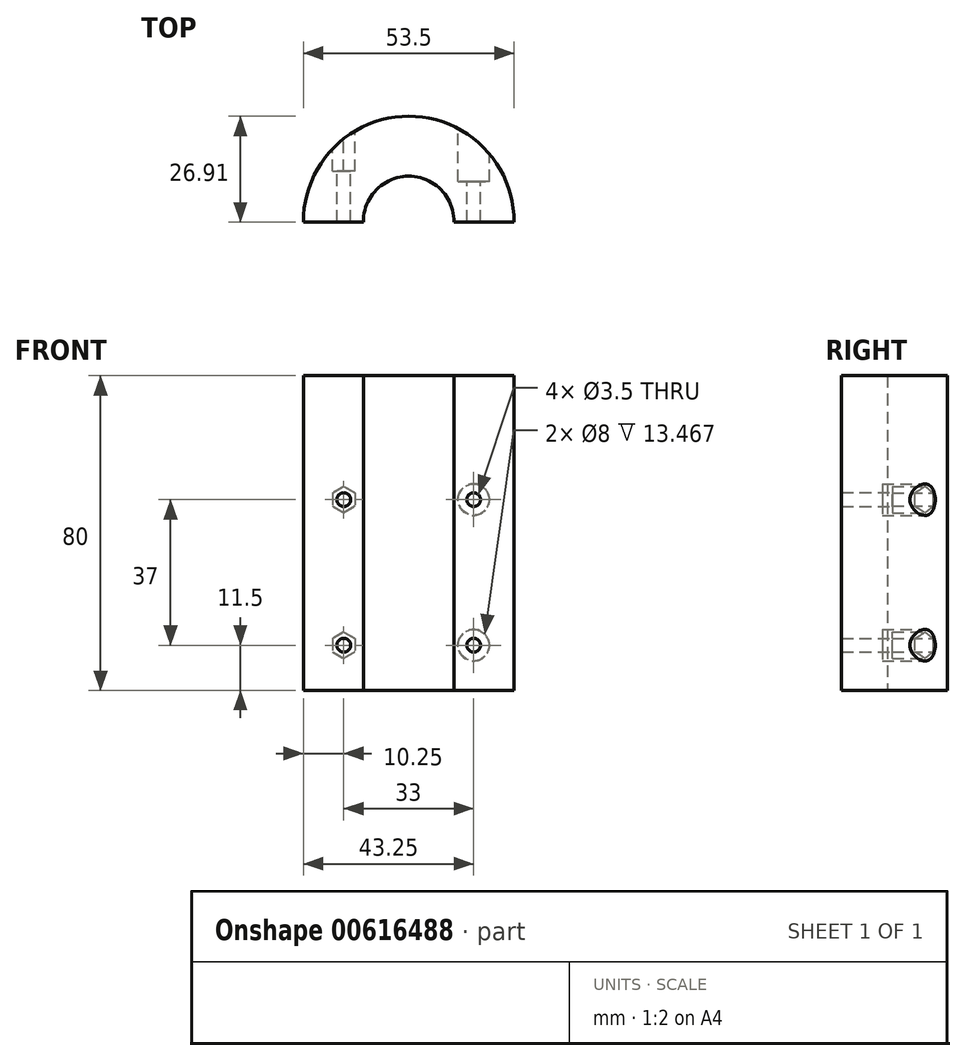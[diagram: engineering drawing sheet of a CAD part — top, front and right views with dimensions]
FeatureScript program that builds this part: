
annotation { "Feature Type Name" : "Feature", "Feature Type Description" : "" }
export const myFeature = defineFeature(function(context is Context, id is Id, definition is map)
    precondition{}
    {
        {
            var Q0;
            Q0=qCreatedBy(makeId("Top.planeOp"),FACE);
            var sketch = newSketch(context, id + "F0", { "sketchPlane" : qUnion([Q0])});
            skArc(sketch, "E0", {"start": v(26.75, -0.16) * mm, "mid": v(0, 26.75) * mm, "end": v(-26.75, -0.16) * mm});
            skArc(sketch, "E1", {"start": v(11.5, -0.16) * mm, "mid": v(0, 11.5) * mm, "end": v(-11.5, -0.16) * mm});
            skLineSegment(sketch, "E2", {"start": v(-26.75, -0.16) * mm, "end": v(-11.5, -0.16) * mm});
            skLineSegment(sketch, "E3.trimOffspring", {"start": v(11.5, -0.16) * mm, "end": v(26.75, -0.16) * mm});
            skSolve(sketch);
        }
        {
            var Q0;
            Q0 = qSketchRegion(id + "F0", true);
            extrude(context, id + "F1", {"entities" : qUnion([Q0]), "depth" : 80 * mm, "offsetDistance" : 25 * mm});
        }
        {
            var Q0;
            Q0=qCreatedBy(makeId("Front.planeOp"),FACE);
            cPlane(context, id + "F2", {"entities" : qUnion([Q0]), "cplaneType" : CPlaneType.OFFSET, "offset" : 26.75 * mm, "oppositeDirection" : true, "width" : 150 * mm, "height" : 150 * mm});
        }
        {
            var Q0;
            Q0=qCreatedBy(id+"F2.planeOp",FACE);
            var sketch = newSketch(context, id + "F3", { "sketchPlane" : qUnion([Q0])});
            skLineSegment(sketch, "E4", {"start": v(0, 0) * mm, "end": v(0, 61.14) * mm, "construction": true});
            skLineSegment(sketch, "E5", {"start": v(19.91, 11.5) * mm, "end": v(-21.03, 11.5) * mm, "construction": true});
            skPoint(sketch, "E6", {"position": v(16.5, 11.5) * mm});
            skLineSegment(sketch, "E7", {"start": v(19.02, 30) * mm, "end": v(-19.41, 30) * mm, "construction": true});
            skPoint(sketch, "E8.MirrorP", {"position": v(16.5, 48.5) * mm});
            skPoint(sketch, "E9.MirrorP", {"position": v(-16.5, 48.5) * mm});
            skPoint(sketch, "E10.MirrorP", {"position": v(-16.5, 11.5) * mm});
            skCircle(sketch, "E11.cCircle", {"center": v(-16.5, 48.5) * mm, "radius": 2.9 * mm, "construction": true});
            skLineSegment(sketch, "E11.0", {"start": v(-13.6, 46.83) * mm, "end": v(-16.5, 45.15) * mm});
            skLineSegment(sketch, "E11.1", {"start": v(-16.5, 45.15) * mm, "end": v(-19.4, 46.83) * mm});
            skLineSegment(sketch, "E11.2", {"start": v(-19.4, 46.83) * mm, "end": v(-19.4, 50.17) * mm});
            skLineSegment(sketch, "E11.3", {"start": v(-19.4, 50.17) * mm, "end": v(-16.5, 51.85) * mm});
            skLineSegment(sketch, "E11.4", {"start": v(-16.5, 51.85) * mm, "end": v(-13.6, 50.17) * mm});
            skLineSegment(sketch, "E11.5", {"start": v(-13.6, 50.17) * mm, "end": v(-13.6, 46.83) * mm});
            skPoint(sketch, "E11.0.midPoint", {"position": v(-15.05, 45.99) * mm});
            skLineSegment(sketch, "E12.MirrorCS", {"start": v(-13.6, 9.83) * mm, "end": v(-13.6, 13.17) * mm});
            skLineSegment(sketch, "E13.MirrorCS", {"start": v(-13.6, 13.17) * mm, "end": v(-16.5, 14.85) * mm});
            skLineSegment(sketch, "E14.MirrorCS", {"start": v(-16.5, 8.15) * mm, "end": v(-13.6, 9.83) * mm});
            skLineSegment(sketch, "E15.MirrorCS", {"start": v(-19.4, 9.83) * mm, "end": v(-16.5, 8.15) * mm});
            skLineSegment(sketch, "E16.MirrorCS", {"start": v(-19.4, 13.17) * mm, "end": v(-19.4, 9.83) * mm});
            skLineSegment(sketch, "E17.MirrorCS", {"start": v(-16.5, 14.85) * mm, "end": v(-19.4, 13.17) * mm});
            skSolve(sketch);
        }
        {
            var Q0;
            Q0=sQuery(id+"F3.wireOp",VERTEX,"E8.MirrorP");
            var Q1;
            Q1=sQuery(id+"F3.wireOp",VERTEX,"E6");
            var Q2;
            Q2=makeQuery(id+"F1.opExtrude","SWEPT_BODY",BODY,{"disambiguationData":[OSD([sQuery(id+"F0.wireOp",EDGE,"E0"),sQuery(id+"F0.wireOp",EDGE,"E1"),sQuery(id+"F0.wireOp",EDGE,"E2"),sQuery(id+"F0.wireOp",EDGE,"E3.trimOffspring")])]});
            hole(context, id + "F4", {"style" : HoleStyle.C_BORE, "endStyle" : HoleEndStyle.THROUGH, "oppositeDirection" : true, "holeDiameter" : 3.5 * mm, "cBoreDiameter" : 8 * mm, "cBoreDepth" : 7 * mm, "majorDiameter" : 5 * mm, "isTappedThrough" : true, "tappedDepth" : 12 * mm, "tapClearance" : 3, "locations" : qUnion([Q0, Q1]), "scope" : qUnion([Q2])});
        }
        {
            var Q0;
            Q0=sQuery(id+"F3.wireOp",VERTEX,"E9.MirrorP");
            var Q1;
            Q1=sQuery(id+"F3.wireOp",VERTEX,"E10.MirrorP");
            var Q2;
            Q2=makeQuery(id+"F1.opExtrude","SWEPT_BODY",BODY,{"disambiguationData":[OSD([sQuery(id+"F0.wireOp",EDGE,"E0"),sQuery(id+"F0.wireOp",EDGE,"E1"),sQuery(id+"F0.wireOp",EDGE,"E2"),sQuery(id+"F0.wireOp",EDGE,"E3.trimOffspring")])]});
            hole(context, id + "F5", {"style" : HoleStyle.SIMPLE, "endStyle" : HoleEndStyle.THROUGH, "oppositeDirection" : true, "holeDiameter" : 3.5 * mm, "majorDiameter" : 5 * mm, "isTappedThrough" : true, "tappedDepth" : 12 * mm, "tapClearance" : 3, "locations" : qUnion([Q0, Q1]), "scope" : qUnion([Q2])});
        }
        {
            var Q0;
            Q0=makeQuery(id+"F3.imprint","IMPRINT",FACE,{"disambiguationData":[TD([[makeQuery(id+"F3.imprint","IMPRINT",EDGE,{"derivedFrom":sQuery(id+"F3.wireOp",EDGE,"E11.0")}),-1.0]])]});
            var Q1;
            Q1=sQuery(id+"F3.wireOp",EDGE,"E11.5");
            var Q2;
            Q2=sQuery(id+"F3.wireOp",EDGE,"E11.0");
            var Q3;
            Q3=sQuery(id+"F3.wireOp",EDGE,"E11.1");
            var Q4;
            Q4=sQuery(id+"F3.wireOp",EDGE,"E11.2");
            var Q5;
            Q5=sQuery(id+"F3.wireOp",EDGE,"E11.3");
            var Q6;
            Q6=sQuery(id+"F3.wireOp",EDGE,"E11.4");
            extrude(context, id + "F6", {"entities" : qUnion([Q0]), "operationType" : NewBodyOperationType.REMOVE, "surfaceEntities" : qUnion([Q1, Q2, Q3, Q4, Q5, Q6]), "oppositeDirection" : true, "depth" : 25 * mm, "offsetDistance" : 25 * mm});
        }
        {
            var Q0;
            Q0=makeQuery(id+"F3.imprint","IMPRINT",FACE,{"disambiguationData":[TD([[makeQuery(id+"F3.imprint","IMPRINT",EDGE,{"derivedFrom":sQuery(id+"F3.wireOp",EDGE,"E11.0")}),-1.0]])]});
            var Q1;
            Q1=makeQuery(id+"F3.imprint","IMPRINT",FACE,{"disambiguationData":[TD([[makeQuery(id+"F3.imprint","IMPRINT",EDGE,{"derivedFrom":sQuery(id+"F3.wireOp",EDGE,"E12.MirrorCS")}),1.0]])]});
            var Q2;
            Q2=sQuery(id+"F3.wireOp",EDGE,"E11.1");
            var Q3;
            Q3=sQuery(id+"F3.wireOp",EDGE,"E11.2");
            var Q4;
            Q4=sQuery(id+"F3.wireOp",EDGE,"E11.0");
            var Q5;
            Q5=sQuery(id+"F3.wireOp",EDGE,"E11.3");
            var Q6;
            Q6=sQuery(id+"F3.wireOp",EDGE,"E11.5");
            var Q7;
            Q7=sQuery(id+"F3.wireOp",EDGE,"E11.4");
            extrude(context, id + "F7", {"entities" : qUnion([Q0, Q1]), "operationType" : NewBodyOperationType.REMOVE, "surfaceEntities" : qUnion([Q2, Q3, Q4, Q5, Q6, Q7]), "depth" : 14 * mm, "offsetDistance" : 25 * mm});
        }
    });
